# Revit family: Shower-Ligature_Resistant-Acorn-Secur-Care-LR1741FA_Series
name_source: partatom
category: Plumbing Fixtures
units: mm (PartAtom-declared; Revit-internal decimal feet)

## family parameters
Cut with Voids When Loaded = Yes
Host = Face
OmniClass Number = 23.45.05.14.17
OmniClass Title = Showers
Part Type = Normal
Room Calculation Point = No
Round Connector Dimension = Use Diameter
Shared = Yes

## types (4) — shared parameters
ADA Compliant = Yes
Assembly Code = D2010710
BRS - Brass Body Valve = No
CW Connection = Yes
CWFU = 3
Cold Water Connection Diameter = 1/2"
Cold Water Connection Radius = 1/4"
Connection Description 1 = 1/2" NPS Upper Showerhead Outlet Connection
Connection Description 2 = 1/2" NPS Lower Showerhead Outlet Connection
Connection Description 4 = 1/2" NPS HW Inlet Connection
Connection Description 5 = 1/2" NPS CW Inlet Connection
Connection Size = 1/2"
Default Elevation = 0"
Description = Secur-Care - Ligature Resistant LR1741FA Series
EG - Enviro-Glaze = No
EVS1 Single Temp = Yes
EVS2 Hot & Cold = No
EVSP1 Single Temp, Piezo Button = No
EVSP2 Hot & Cold, Piezo Buttons = No
F - Flow Control 2.0 GPM = No
Flow Rate = 1.6 GPM
HW Connection = Yes
HWFU = 3
Height = 20"
Hot Water Connection Diameter = 1/2"
Hot Water Connection Radius = 1/4"
IAPMO Compliance = Mixing Valve meets criteria for temperature and pressure changes,
defined by ASSE 1016. Valve conforms with lead free requirements of NSF61, Section 9, 1997 and CHSC 116875.
Installation Instruction Link = https://www.acorneng.com
Installation Type = Recessed Wall Mounted
Length = 4 3/8"
MTP1 - Single Temp = No
MTP2 - Hot & Cold = No
MTPP1 - Single Temp, Piezo Button = No
MTPP2 - Hot & Cold, Piezo Buttons = No
MVC1 - Time-Trol - Single Temp = No
MVC2 - Time-Trol - Hot & Cold = Yes
Manufacturer = Acorn Engineering
Material = Metal-Whitehall-304-Stainless_Steel-16_Gauge
PPZ1 Single Temp Programmable Piezo Button = No
PPZ2 - Programmable Piezo Button (Hot and Cold) = No
Price = Prices may vary. Please consult Manufacturer Representative for most up-to-date price list.
Product Documentation Link = https://www.acorneng.com
Product Page URL = https://www.acorneng.com
TF - 120VAC to 24VAC Transformer = No
Tempered Water Connection = Yes
Tempered Water Connection Diameter = 1/2"
URL = https://www.acorneng.com
Vent Connection = No
Waste Connection = No
Width = 10"
zero-valued in all types: WFU

## per-type parameters (varying)
| type | 03-M-MA2 Manifolded Single Temp, Metering | 04-M-MA2 Manifolded Hot & Cold, Metering | LRD - Less Recessed Soap Dish | RD - Recessed Soap Dish | Shower Options |
| LR1741FA-03-M-RD | Yes | No | No | Yes | -LR1741FA-RD |
| LR1741FA-03-M-LRD | Yes | No | Yes | No | -LR1741FA-LRD |
| LR1741FA-04-M-LRD | No | Yes | Yes | No | -LR1741FA-4-LRD |
| LR1741FA-04-M-RD | No | Yes | No | Yes | -LR1741FA-4-RD |

note: column(s) folded — value = type name in every type: Model

## geometry (parser evidence)
native form markers: Sweep x16
no freeform markers — native parametric forms only
